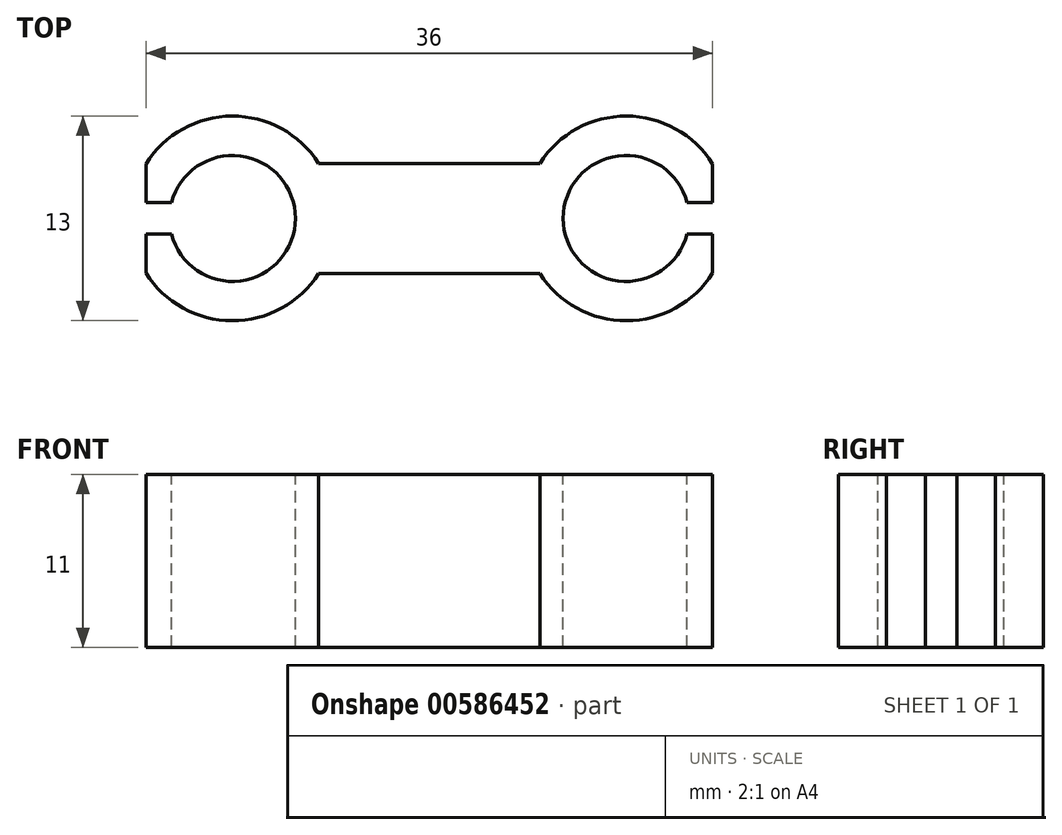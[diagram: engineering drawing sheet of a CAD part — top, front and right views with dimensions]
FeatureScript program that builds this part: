
annotation { "Feature Type Name" : "Feature", "Feature Type Description" : "" }
export const myFeature = defineFeature(function(context is Context, id is Id, definition is map)
    precondition{}
    {
        {
            var Q0;
            Q0=qCreatedBy(makeId("Top.planeOp"),FACE);
            var sketch = newSketch(context, id + "F0", { "sketchPlane" : qUnion([Q0])});
            skLineSegment(sketch, "E0.bottom", {"start": v(12.5, 3.5) * mm, "end": v(-12.5, 3.5) * mm});
            skLineSegment(sketch, "E0.top", {"start": v(12.5, -3.5) * mm, "end": v(-12.5, -3.5) * mm});
            skLineSegment(sketch, "E0.left", {"start": v(12.5, 3.5) * mm, "end": v(12.5, -3.5) * mm});
            skLineSegment(sketch, "E0.right", {"start": v(-12.5, 3.5) * mm, "end": v(-12.5, -3.5) * mm});
            skPoint(sketch, "E0.middle", {"position": v(0, 0) * mm});
            skCircle(sketch, "E1", {"center": v(12.5, 0) * mm, "radius": 6.5 * mm});
            skCircle(sketch, "E2", {"center": v(-12.5, 0) * mm, "radius": 6.5 * mm});
            skSolve(sketch);
        }
        {
            var Q0;
            {var subQ0=sQuery(id+"F0.wireOp",EDGE,"E0.right");Q0=makeQuery(id+"F0.imprint","IMPRINT",FACE,{"disambiguationData":[TD([[makeQuery(id+"F0.imprint","IMPRINT",EDGE,{"derivedFrom":subQ0}),-1.0]])]});}
            var Q1;
            {var subQ0=sQuery(id+"F0.wireOp",EDGE,"E1");var subQ1=sQuery(id+"F0.wireOp",EDGE,"E0.bottom");var subQ2=makeQuery(id+"F0.imprint","INTERSECT",VERTEX,{"derivedFrom":[subQ1,subQ0]});Q1=makeQuery(id+"F0.imprint","IMPRINT",FACE,{"disambiguationData":[TD([[makeQuery(id+"F0.imprint","IMPRINT",EDGE,{"disambiguationData":[TD([[subQ2,-1.0]])],"derivedFrom":subQ1}),1.0]])]});}
            var Q2;
            {var subQ0=sQuery(id+"F0.wireOp",EDGE,"E0.left");Q2=makeQuery(id+"F0.imprint","IMPRINT",FACE,{"disambiguationData":[TD([[makeQuery(id+"F0.imprint","IMPRINT",EDGE,{"derivedFrom":subQ0}),1.0]])]});}
            var Q3;
            {var subQ0=sQuery(id+"F0.wireOp",EDGE,"E0.right");Q3=makeQuery(id+"F0.imprint","IMPRINT",FACE,{"disambiguationData":[TD([[makeQuery(id+"F0.imprint","IMPRINT",EDGE,{"derivedFrom":subQ0}),1.0]])]});}
            var Q4;
            {var subQ0=sQuery(id+"F0.wireOp",EDGE,"E0.left");Q4=makeQuery(id+"F0.imprint","IMPRINT",FACE,{"disambiguationData":[TD([[makeQuery(id+"F0.imprint","IMPRINT",EDGE,{"derivedFrom":subQ0}),-1.0]])]});}
            extrude(context, id + "F1", {"entities" : qUnion([Q0, Q1, Q2, Q3, Q4]), "depth" : 11 * mm, "offsetDistance" : 25 * mm});
        }
        {
            var Q0;
            Q0=makeQuery(id+"F1.opExtrude","CAP_FACE",FACE,{"disambiguationData":[OSD([sQuery(id+"F0.wireOp",EDGE,"E0.bottom"),sQuery(id+"F0.wireOp",EDGE,"E0.top"),sQuery(id+"F0.wireOp",EDGE,"E1"),sQuery(id+"F0.wireOp",EDGE,"E2")])],"isStart":false});
            var sketch = newSketch(context, id + "F2", { "sketchPlane" : qUnion([Q0])});
            skCircle(sketch, "E3", {"center": v(-12.5, 0) * mm, "radius": 4 * mm});
            skCircle(sketch, "E4", {"center": v(12.5, 0) * mm, "radius": 4 * mm});
            skLineSegment(sketch, "E5.bottom", {"start": v(-16, 1) * mm, "end": v(-22, 1) * mm});
            skLineSegment(sketch, "E5.top", {"start": v(-16, -1) * mm, "end": v(-22, -1) * mm});
            skLineSegment(sketch, "E5.left", {"start": v(-16, 1) * mm, "end": v(-16, -1) * mm});
            skLineSegment(sketch, "E5.right", {"start": v(-22, 1) * mm, "end": v(-22, -1) * mm});
            skPoint(sketch, "E5.middle", {"position": v(-19, 0) * mm});
            skLineSegment(sketch, "E6.bottom", {"start": v(22, 1) * mm, "end": v(16, 1) * mm});
            skLineSegment(sketch, "E6.top", {"start": v(22, -1) * mm, "end": v(16, -1) * mm});
            skLineSegment(sketch, "E6.left", {"start": v(22, 1) * mm, "end": v(22, -1) * mm});
            skLineSegment(sketch, "E6.right", {"start": v(16, 1) * mm, "end": v(16, -1) * mm});
            skPoint(sketch, "E6.middle", {"position": v(19, 0) * mm});
            skLineSegment(sketch, "E7.bottom", {"start": v(-20, 4) * mm, "end": v(-18, 4) * mm});
            skLineSegment(sketch, "E7.top", {"start": v(-20, -4) * mm, "end": v(-18, -4) * mm});
            skLineSegment(sketch, "E7.left", {"start": v(-20, 4) * mm, "end": v(-20, -4) * mm});
            skLineSegment(sketch, "E7.right", {"start": v(-18, 4) * mm, "end": v(-18, -4) * mm});
            skLineSegment(sketch, "E8.bottom", {"start": v(20, 4) * mm, "end": v(18, 4) * mm});
            skLineSegment(sketch, "E8.top", {"start": v(20, -4) * mm, "end": v(18, -4) * mm});
            skLineSegment(sketch, "E8.left", {"start": v(20, 4) * mm, "end": v(20, -4) * mm});
            skLineSegment(sketch, "E8.right", {"start": v(18, 4) * mm, "end": v(18, -4) * mm});
            skSolve(sketch);
        }
        {
            var Q0;
            {var subQ0=sQuery(id+"F2.wireOp",EDGE,"E5.bottom");var subQ1=sQuery(id+"F2.wireOp",EDGE,"E3");var subQ2=makeQuery(id+"F2.imprint","INTERSECT",VERTEX,{"derivedFrom":[subQ1,subQ0]});Q0=makeQuery(id+"F2.imprint","IMPRINT",FACE,{"disambiguationData":[TD([[makeQuery(id+"F2.imprint","IMPRINT",EDGE,{"disambiguationData":[TD([[subQ2,-1.0]])],"derivedFrom":subQ1}),-1.0]])]});}
            var Q1;
            {var subQ5=sQuery(id+"F2.wireOp",EDGE,"E5.left");Q1=makeQuery(id+"F2.imprint","IMPRINT",FACE,{"disambiguationData":[TD([[makeQuery(id+"F2.imprint","IMPRINT",EDGE,{"derivedFrom":subQ5}),1.0]])]});}
            var Q2;
            {var subQ5=sQuery(id+"F2.wireOp",EDGE,"E5.left");Q2=makeQuery(id+"F2.imprint","IMPRINT",FACE,{"disambiguationData":[TD([[makeQuery(id+"F2.imprint","IMPRINT",EDGE,{"derivedFrom":subQ5}),-1.0]])]});}
            var Q3;
            {var subQ5=sQuery(id+"F2.wireOp",EDGE,"E6.right");Q3=makeQuery(id+"F2.imprint","IMPRINT",FACE,{"disambiguationData":[TD([[makeQuery(id+"F2.imprint","IMPRINT",EDGE,{"derivedFrom":subQ5}),1.0]])]});}
            var Q4;
            {var subQ0=sQuery(id+"F2.wireOp",EDGE,"E6.bottom");var subQ1=sQuery(id+"F2.wireOp",EDGE,"E4");var subQ2=makeQuery(id+"F2.imprint","INTERSECT",VERTEX,{"derivedFrom":[subQ1,subQ0]});Q4=makeQuery(id+"F2.imprint","IMPRINT",FACE,{"disambiguationData":[TD([[makeQuery(id+"F2.imprint","IMPRINT",EDGE,{"disambiguationData":[TD([[subQ2,1.0]])],"derivedFrom":subQ1}),-1.0]])]});}
            var Q5;
            {var subQ5=sQuery(id+"F2.wireOp",EDGE,"E6.right");Q5=makeQuery(id+"F2.imprint","IMPRINT",FACE,{"disambiguationData":[TD([[makeQuery(id+"F2.imprint","IMPRINT",EDGE,{"derivedFrom":subQ5}),-1.0]])]});}
            var Q6;
            {var subQ0=sQuery(id+"F2.wireOp",EDGE,"E7.right");var subQ1=sQuery(id+"F2.wireOp",EDGE,"E5.bottom");var subQ2=makeQuery(id+"F2.imprint","INTERSECT",VERTEX,{"derivedFrom":[subQ1,subQ0]});Q6=makeQuery(id+"F2.imprint","IMPRINT",FACE,{"disambiguationData":[TD([[makeQuery(id+"F2.imprint","IMPRINT",EDGE,{"disambiguationData":[TD([[subQ2,-1.0]])],"derivedFrom":subQ1}),1.0]])]});}
            var Q7;
            {var subQ0=sQuery(id+"F2.wireOp",EDGE,"E8.right");var subQ1=sQuery(id+"F2.wireOp",EDGE,"E6.bottom");var subQ2=makeQuery(id+"F2.imprint","INTERSECT",VERTEX,{"derivedFrom":[subQ1,subQ0]});Q7=makeQuery(id+"F2.imprint","IMPRINT",FACE,{"disambiguationData":[TD([[makeQuery(id+"F2.imprint","IMPRINT",EDGE,{"disambiguationData":[TD([[subQ2,1.0]])],"derivedFrom":subQ1}),1.0]])]});}
            var Q8;
            {var subQ0=sQuery(id+"F2.wireOp",EDGE,"E8.right");var subQ1=sQuery(id+"F2.wireOp",EDGE,"E6.bottom");var subQ2=makeQuery(id+"F2.imprint","INTERSECT",VERTEX,{"derivedFrom":[subQ1,subQ0]});Q8=makeQuery(id+"F2.imprint","IMPRINT",FACE,{"disambiguationData":[TD([[makeQuery(id+"F2.imprint","IMPRINT",EDGE,{"disambiguationData":[TD([[subQ2,1.0]])],"derivedFrom":subQ1}),-1.0]])]});}
            var Q9;
            {var subQ0=sQuery(id+"F2.wireOp",EDGE,"E8.right");var subQ1=sQuery(id+"F2.wireOp",EDGE,"E6.top");var subQ2=makeQuery(id+"F2.imprint","INTERSECT",VERTEX,{"derivedFrom":[subQ1,subQ0]});Q9=makeQuery(id+"F2.imprint","IMPRINT",FACE,{"disambiguationData":[TD([[makeQuery(id+"F2.imprint","IMPRINT",EDGE,{"disambiguationData":[TD([[subQ2,1.0]])],"derivedFrom":subQ1}),1.0]])]});}
            var Q10;
            {var subQ0=sQuery(id+"F2.wireOp",EDGE,"E7.right");var subQ1=sQuery(id+"F2.wireOp",EDGE,"E5.bottom");var subQ2=makeQuery(id+"F2.imprint","INTERSECT",VERTEX,{"derivedFrom":[subQ1,subQ0]});Q10=makeQuery(id+"F2.imprint","IMPRINT",FACE,{"disambiguationData":[TD([[makeQuery(id+"F2.imprint","IMPRINT",EDGE,{"disambiguationData":[TD([[subQ2,-1.0]])],"derivedFrom":subQ1}),-1.0]])]});}
            var Q11;
            {var subQ0=sQuery(id+"F2.wireOp",EDGE,"E7.right");var subQ1=sQuery(id+"F2.wireOp",EDGE,"E5.top");var subQ2=makeQuery(id+"F2.imprint","INTERSECT",VERTEX,{"derivedFrom":[subQ1,subQ0]});Q11=makeQuery(id+"F2.imprint","IMPRINT",FACE,{"disambiguationData":[TD([[makeQuery(id+"F2.imprint","IMPRINT",EDGE,{"disambiguationData":[TD([[subQ2,-1.0]])],"derivedFrom":subQ1}),1.0]])]});}
            extrude(context, id + "F3", {"entities" : qUnion([Q0, Q1, Q2, Q3, Q4, Q5, Q6, Q7, Q8, Q9, Q10, Q11]), "operationType" : NewBodyOperationType.REMOVE, "endBound" : BoundingType.UP_TO_NEXT, "oppositeDirection" : true, "depth" : 25 * mm, "offsetDistance" : 25 * mm});
        }
    });
